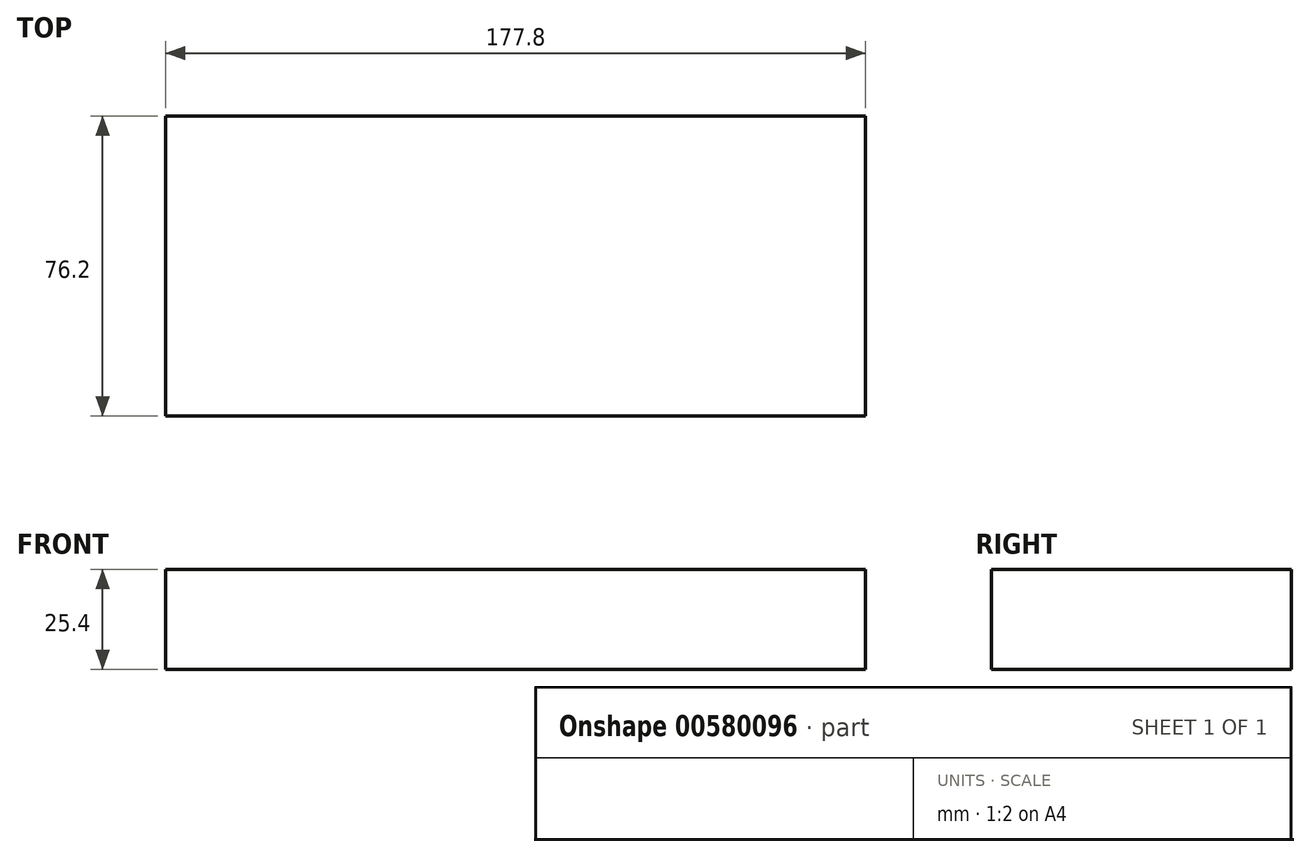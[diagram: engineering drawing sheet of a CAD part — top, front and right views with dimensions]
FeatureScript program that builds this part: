
annotation { "Feature Type Name" : "Feature", "Feature Type Description" : "" }
export const myFeature = defineFeature(function(context is Context, id is Id, definition is map)
    precondition{}
    {
        {
            var Q0;
            Q0=qCreatedBy(makeId("Top.planeOp"),FACE);
            var sketch = newSketch(context, id + "F0", { "sketchPlane" : qUnion([Q0])});
            skLineSegment(sketch, "E0.bottom", {"start": v(-88.9, 38.1) * mm, "end": v(88.9, 38.1) * mm});
            skLineSegment(sketch, "E0.top", {"start": v(-88.9, -38.1) * mm, "end": v(88.9, -38.1) * mm});
            skLineSegment(sketch, "E0.left", {"start": v(-88.9, 38.1) * mm, "end": v(-88.9, -38.1) * mm});
            skLineSegment(sketch, "E0.right", {"start": v(88.9, 38.1) * mm, "end": v(88.9, -38.1) * mm});
            skPoint(sketch, "E0.middle", {"position": v(0, 0) * mm});
            skSolve(sketch);
        }
        {
            var Q0;
            Q0=qSketchRegion(id+"F0",true);
            extrude(context, id + "F1", {"entities" : qUnion([Q0]), "depth" : 25.4 * mm});
        }
    });
